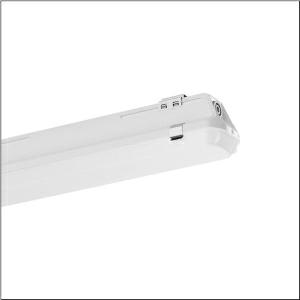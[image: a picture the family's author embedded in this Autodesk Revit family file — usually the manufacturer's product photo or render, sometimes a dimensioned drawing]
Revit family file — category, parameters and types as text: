
# Revit family: monsun_r__21_51fb207p430j_73f4
name_source: partatom
category: Lighting Fixtures
units: mm (PartAtom-declared; Revit-internal decimal feet)

## family parameters
Cut with Voids When Loaded = No
Host = Face
Light Source = No
Part Type = Normal
Room Calculation Point = No
Round Connector Dimension = Use Diameter
Shared = No

## types (1)
- Monsun® 21 (1 x LED, 3340 lm, 22.2 W, 4000K)
    Apparent Load = 22 VA
    CIE Flux Codes = 45 75 93 94 100
    Color Rendering = 80
    Color Temperature = 4000K
    Default Elevation = 1800 mm
    Description = Monsun® 21, damp-proof luminaire, chain hanger, primary optical cover: enclosure, of PC, light emission: direct distribution, primary light characteristic: symmetric, installation type: suspended mounting, surface-mounted, horizontal mounting, vertical mounting, LED, rated luminous flux: 3.340lm, luminous efficacy: 150lm/W, light colour: 840, colour temperature: 4000K, control gear: ECG, with terminal, 3-pole, max. 2.5mm², mains connection: 220..240V, AC, 50/60Hz, rated input power: 22W, housing, of glass-fibre reinforced polyester, uncoated, bright grey, incl. chain hanger, length: 1.590mm, width: 90mm, height: 88mm, clip for enclosure, of stainless steel (V2A), ceiling mounting element, of stainless steel (V2A), chain hanger, of stainless steel (V2A), protection rating (complete): IP66, insulation class (complete): insulation class I (protective earthing), certification: CE, ENEC, VDE, UKCA, protection symbol: D, impact resistance: IK08, permissible operating ambient temperature: -25..+35°C, standard: EN 50419, EN 60598-2-1, corresponds to IFS (International Featured Standards) requirements for safety and quality in the food industry, for indoor or canopied outdoor use, no direct snow, no direct sun, no direct rain, contact your sales advisor before using the luminaires in applications with unclear chemical exposure, large temperature fluctuations or condensation-forming humidity, LABS conformity tested according to VDMA 24364:2018-05, packaging unit: 1 piece
    Height = 89 mm
    Lamp = 1 x LED
    Lamp Light Flux = 3340 lm
    Lamp Power = 22.2 W
    Lamp count = 1
    Length = 1590 mm
    Luminous efficacy = 150 lm/W
    Manufacturer = Siteco
    ModVariant = No
    Model = 51FB207P430J
    Mounting Place = Ceiling
    Mounting Type = Surface mounted
    Number of Poles = 1
    OnlyDefault = Yes
    Power Factor = 1
    Product Name = Monsun® 21
    Product group = damp-proof luminaire
    ProductGroupID = 300
    Protection Class = Protection class I
    Protection Degree = IP 66
    RLX_Detail_Level = 1
    RLX_Emergency_Light_Flux = 0 lm
    RLX_Emergency_Type = 0
    RLX_Emergency_Type_DB = No
    RlxData = <blob elided: 88345 chars, md5=bde6ea4a>
    Socket = socket
    Standby Power = 0 W
    System Light Flux = 3340 lm
    System Power = 22 W
    Type Comments = Product without accessories
    Type Image = l_1006717.jpg
    URL = http://relux.com
    VarID = ---
    Voltage = 0 V
    Weight = 0.00 kg
    Width = 90 mm

## geometry (parser evidence)
native form markers: Blend x4, Sweep x15
no freeform markers — native parametric forms only
